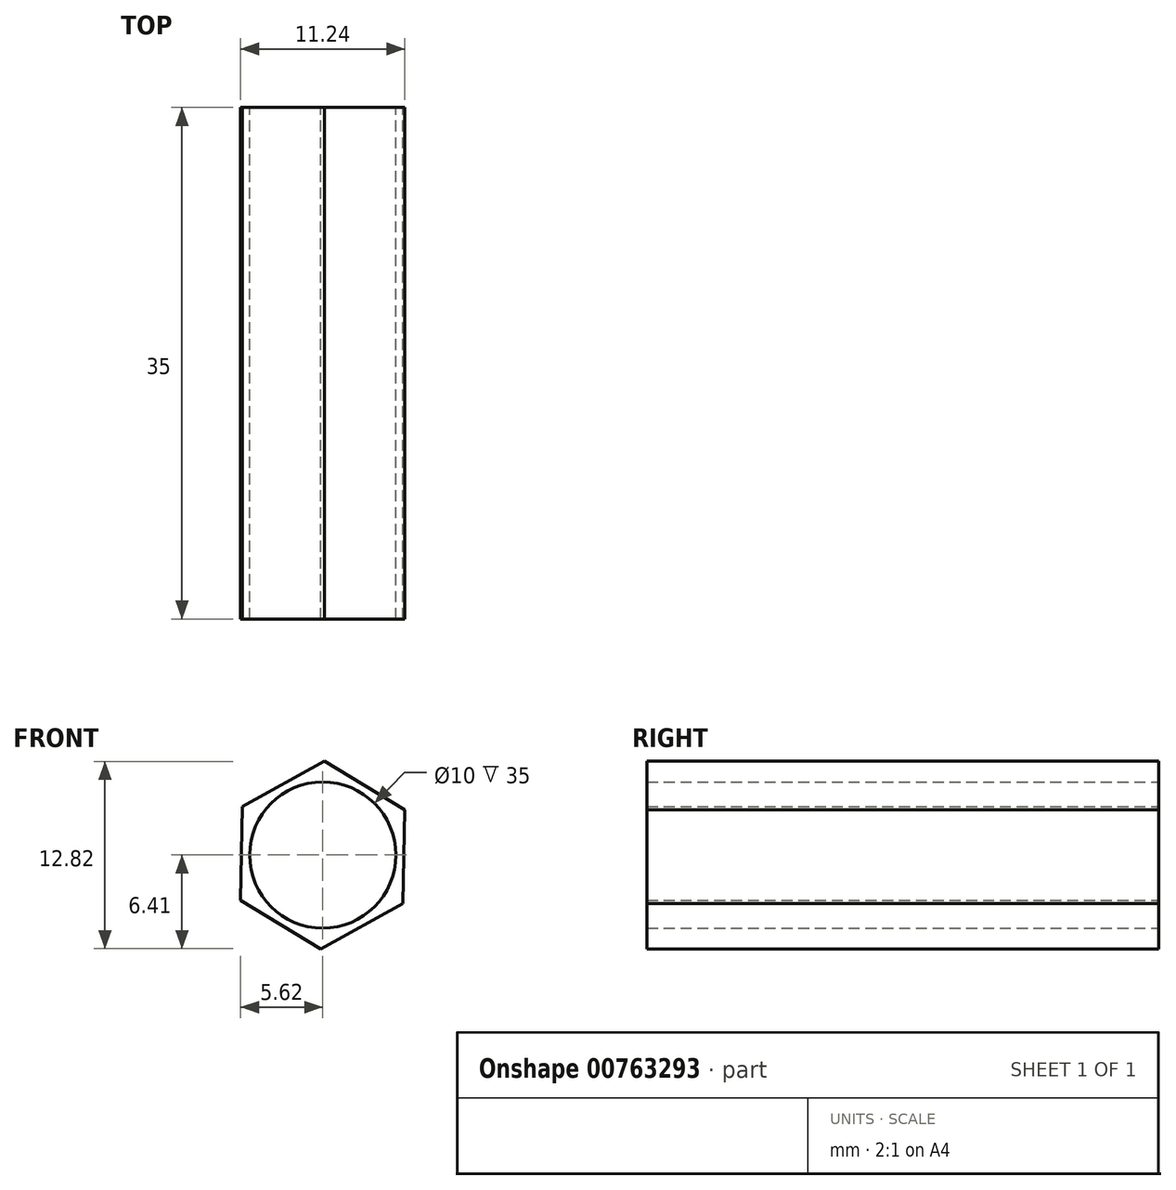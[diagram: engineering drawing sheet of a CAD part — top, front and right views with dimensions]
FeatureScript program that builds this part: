
annotation { "Feature Type Name" : "Feature", "Feature Type Description" : "" }
export const myFeature = defineFeature(function(context is Context, id is Id, definition is map)
    precondition{}
    {
        {
            var Q0;
            Q0=qCreatedBy(makeId("Front.planeOp"),FACE);
            var sketch = newSketch(context, id + "F0", { "sketchPlane" : qUnion([Q0])});
            skCircle(sketch, "E0.cCircle", {"center": v(0, 0) * mm, "radius": 5.56 * mm, "construction": true});
            skLineSegment(sketch, "E0.0", {"start": v(-0.13, -6.41) * mm, "end": v(-5.62, -3.1) * mm});
            skLineSegment(sketch, "E0.1", {"start": v(-5.62, -3.1) * mm, "end": v(-5.49, 3.32) * mm});
            skLineSegment(sketch, "E0.2", {"start": v(-5.49, 3.32) * mm, "end": v(0.13, 6.41) * mm});
            skLineSegment(sketch, "E0.3", {"start": v(0.13, 6.41) * mm, "end": v(5.62, 3.1) * mm});
            skLineSegment(sketch, "E0.4", {"start": v(5.62, 3.1) * mm, "end": v(5.49, -3.32) * mm});
            skLineSegment(sketch, "E0.5", {"start": v(5.49, -3.32) * mm, "end": v(-0.13, -6.41) * mm});
            skPoint(sketch, "E0.0.midPoint", {"position": v(-2.88, -4.75) * mm});
            skCircle(sketch, "E1", {"center": v(0, 0) * mm, "radius": 5 * mm});
            skSolve(sketch);
        }
        {
            var Q0;
            Q0 = qSketchRegion(id + "F0", true);
            extrude(context, id + "F1", {"entities" : qUnion([Q0]), "depth" : 35 * mm, "offsetDistance" : 25 * mm});
        }
    });
